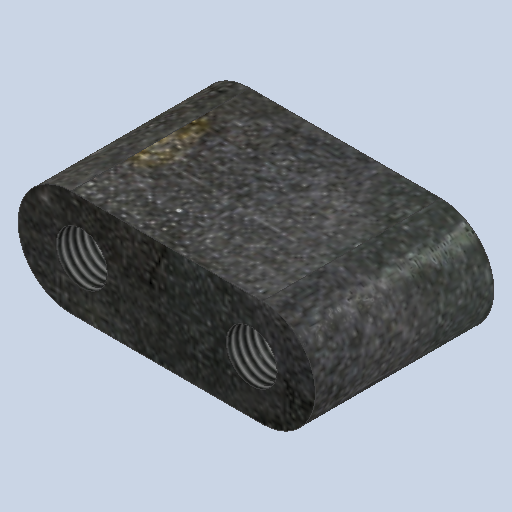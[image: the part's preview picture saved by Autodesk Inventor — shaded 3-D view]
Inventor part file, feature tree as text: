
AUTODESK INVENTOR PART (.ipt)
format: ipt  version: 2024 (Build 280153000, 153)  size: 315,392 bytes
history: native  units: mm
features: extrude x2, other x2, thread x2, sketch x2
ambient origin geometry x8: Origin, YZ Plane, XZ Plane, XY Plane, X Axis, Y Axis, Z Axis, Center Point
bodies: Solid1 (feature_tree)
feature tree (8):
  extrude  "Extrusion1"  Depth=25.0mm
  other  "Full Round Fillet1"
  other  "Full Round Fillet2"
  extrude  "Extrusion2"  Depth=12.5mm
  thread  "Thread1"  [1 undecoded]
  thread  "Thread2"  [1 undecoded]
  sketch  "Sketch1"  dims[d0=70.0mm d1=25.0mm]
  sketch  "Sketch2"  dims[d2=35.0mm d3=12.5mm d4=42.0mm d5=0.0mm d6=12.0mm d7=12.0mm d8=40.0mm d9=20.0mm d10=42.0mm d11=0.0mm d12=42.0mm d13=0.0mm d14=42.0mm d15=0.0mm]
note: 2 required parameter values undecoded (feature->parameter linkage not recoverable at this tier; creation-order binding heuristic only, values carry confidence <= 0.55)
